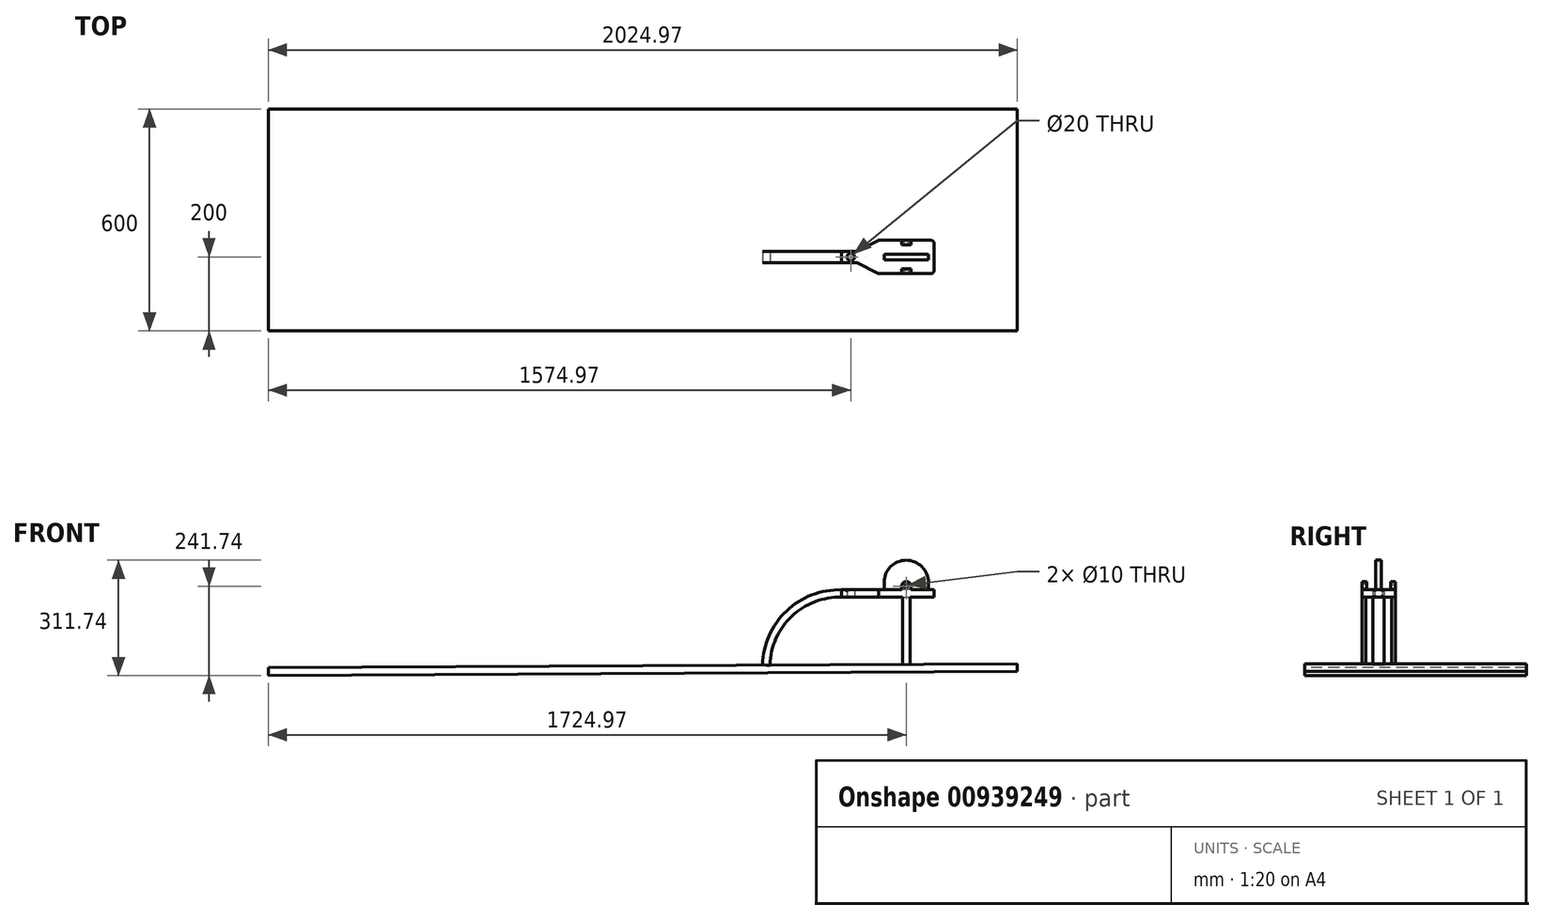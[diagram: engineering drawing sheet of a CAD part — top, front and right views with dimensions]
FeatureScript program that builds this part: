
annotation { "Feature Type Name" : "Feature", "Feature Type Description" : "" }
export const myFeature = defineFeature(function(context is Context, id is Id, definition is map)
    precondition{}
    {
        {
            var Q0;
            Q0=qCreatedBy(makeId("Right.planeOp"),FACE);
            var sketch = newSketch(context, id + "F0", { "sketchPlane" : qUnion([Q0])});
            skLineSegment(sketch, "E0", {"start": v(0, 10) * mm, "end": v(45, 10) * mm});
            skLineSegment(sketch, "E1", {"start": v(45, 10) * mm, "end": v(45, -10) * mm});
            skLineSegment(sketch, "E2", {"start": v(45, -10) * mm, "end": v(-45, -10) * mm});
            skLineSegment(sketch, "E3", {"start": v(-45, -10) * mm, "end": v(-45, 10) * mm});
            skLineSegment(sketch, "E4", {"start": v(-45, 10) * mm, "end": v(0, 10) * mm});
            skSolve(sketch);
        }
        {
            var Q0;
            Q0=makeQuery(id+"F0.imprint","IMPRINT",FACE,{"disambiguationData":[TD([[makeQuery(id+"F0.imprint","IMPRINT",EDGE,{"derivedFrom":sQuery(id+"F0.wireOp",EDGE,"E0")}),-1.0]])]});
            extrude(context, id + "F1", {"entities" : qUnion([Q0]), "depth" : 150 * mm, "offsetDistance" : 25 * mm});
        }
        {
            var Q0;
            Q0=makeQuery(id+"F1.opExtrude","SWEPT_FACE",FACE,{"disambiguationData":[OSD([sQuery(id+"F0.wireOp",EDGE,"E3")])]});
            cPlane(context, id + "F2", {"entities" : qUnion([Q0]), "cplaneType" : CPlaneType.OFFSET, "offset" : 0 * mm, "width" : 150 * mm, "height" : 150 * mm});
        }
        {
            var Q0;
            Q0=qCreatedBy(id+"F2.planeOp",FACE);
            var sketch = newSketch(context, id + "F3", { "sketchPlane" : qUnion([Q0])});
            skLineSegment(sketch, "E5", {"start": v(0, 0) * mm, "end": v(75, 0) * mm});
            skLineSegment(sketch, "E6", {"start": v(75, 0) * mm, "end": v(75, 10) * mm});
            skArc(sketch, "E7", {"start": v(87.5, 20) * mm, "mid": v(75, 32.5) * mm, "end": v(62.5, 20) * mm});
            skLineSegment(sketch, "E8", {"start": v(87.5, 20) * mm, "end": v(87.5, 10) * mm});
            skLineSegment(sketch, "E9", {"start": v(62.5, 20) * mm, "end": v(62.5, 10) * mm});
            skLineSegment(sketch, "E10", {"start": v(62.5, 10) * mm, "end": v(87.5, 10) * mm});
            skCircle(sketch, "E11", {"center": v(75, 20) * mm, "radius": 5 * mm});
            skSolve(sketch);
        }
        {
            var Q0;
            Q0=makeQuery(id+"F3.imprint","IMPRINT",FACE,{"disambiguationData":[TD([[makeQuery(id+"F3.imprint","IMPRINT",EDGE,{"derivedFrom":sQuery(id+"F3.wireOp",EDGE,"E7")}),1.0]])]});
            extrude(context, id + "F4", {"entities" : qUnion([Q0]), "operationType" : NewBodyOperationType.ADD, "oppositeDirection" : true, "depth" : 12.5 * mm, "offsetDistance" : 25 * mm});
        }
        {
            var Q0;
            Q0=makeQuery(id+"F1.opExtrude","SWEPT_FACE",FACE,{"disambiguationData":[OSD([sQuery(id+"F0.wireOp",EDGE,"E1")])]});
            cPlane(context, id + "F5", {"entities" : qUnion([Q0]), "cplaneType" : CPlaneType.OFFSET, "offset" : 0 * mm, "width" : 150 * mm, "height" : 150 * mm});
        }
        {
            var Q0;
            Q0=qCreatedBy(id+"F5.planeOp",FACE);
            var sketch = newSketch(context, id + "F6", { "sketchPlane" : qUnion([Q0])});
            skLineSegment(sketch, "E12", {"start": v(0, 0) * mm, "end": v(-75, 0) * mm});
            skLineSegment(sketch, "E13", {"start": v(-75, 0) * mm, "end": v(-75, 10) * mm});
            skArc(sketch, "E14", {"start": v(-62.5, 20) * mm, "mid": v(-75, 32.5) * mm, "end": v(-87.5, 20) * mm});
            skCircle(sketch, "E15", {"center": v(-75, 20) * mm, "radius": 5 * mm});
            skLineSegment(sketch, "E16", {"start": v(-87.5, 20) * mm, "end": v(-87.5, 10) * mm});
            skLineSegment(sketch, "E17", {"start": v(-62.5, 20) * mm, "end": v(-62.5, 10) * mm});
            skLineSegment(sketch, "E18", {"start": v(-87.5, 10) * mm, "end": v(-62.5, 10) * mm});
            skSolve(sketch);
        }
        {
            var Q0;
            Q0=makeQuery(id+"F6.imprint","IMPRINT",FACE,{"disambiguationData":[TD([[makeQuery(id+"F6.imprint","IMPRINT",EDGE,{"derivedFrom":sQuery(id+"F6.wireOp",EDGE,"E14")}),1.0]])]});
            extrude(context, id + "F7", {"entities" : qUnion([Q0]), "operationType" : NewBodyOperationType.ADD, "oppositeDirection" : true, "depth" : 12.5 * mm, "offsetDistance" : 25 * mm});
        }
        {
            var Q0;
            Q0=qCreatedBy(id+"F5.planeOp",FACE);
            cPlane(context, id + "F8", {"entities" : qUnion([Q0]), "cplaneType" : CPlaneType.OFFSET, "offset" : 45 * mm, "oppositeDirection" : true, "width" : 150 * mm, "height" : 150 * mm});
        }
        {
            var Q0;
            Q0=qCreatedBy(id+"F8.planeOp",FACE);
            var sketch = newSketch(context, id + "F9", { "sketchPlane" : qUnion([Q0])});
            skLineSegment(sketch, "E19", {"start": v(0, 0) * mm, "end": v(-75, 0) * mm});
            skLineSegment(sketch, "E20", {"start": v(-75, 0) * mm, "end": v(-75, 10) * mm});
            skLineSegment(sketch, "E21", {"start": v(-15, 30) * mm, "end": v(-15, 10) * mm});
            skLineSegment(sketch, "E22", {"start": v(-135, 30) * mm, "end": v(-135, 10) * mm});
            skLineSegment(sketch, "E23", {"start": v(-135, 10) * mm, "end": v(-15, 10) * mm});
            skArc(sketch, "E24.trimOffspring", {"start": v(-15, 30) * mm, "mid": v(-75, 90) * mm, "end": v(-135, 30) * mm});
            skSolve(sketch);
        }
        {
            var Q0;
            {var subQ2=sQuery(id+"F9.wireOp",EDGE,"E21");Q0=makeQuery(id+"F9.imprint","IMPRINT",FACE,{"disambiguationData":[TD([[makeQuery(id+"F9.imprint","IMPRINT",EDGE,{"derivedFrom":subQ2}),-1.0]])]});}
            extrude(context, id + "F10", {"entities" : qUnion([Q0]), "operationType" : NewBodyOperationType.ADD, "depth" : 7.5 * mm, "offsetDistance" : 25 * mm, "hasSecondDirection" : true, "secondDirectionOppositeDirection" : true, "secondDirectionDepth" : 7.5 * mm});
        }
        {
            var Q0;
            Q0=qCreatedBy(id+"F8.planeOp",FACE);
            var sketch = newSketch(context, id + "F11", { "sketchPlane" : qUnion([Q0])});
            skLineSegment(sketch, "E25", {"start": v(0, 0) * mm, "end": v(-75, 0) * mm});
            skLineSegment(sketch, "E26", {"start": v(-375, -190) * mm, "end": v(-375, -210) * mm});
            skLineSegment(sketch, "E27", {"start": v(1649.97, -200) * mm, "end": v(1649.84, -221.74) * mm});
            skLineSegment(sketch, "E28", {"start": v(-375, -210) * mm, "end": v(1649.84, -221.74) * mm});
            skLineSegment(sketch, "E29", {"start": v(1649.97, -200) * mm, "end": v(-375, -190) * mm});
            skLineSegment(sketch, "E30", {"start": v(0, 0) * mm, "end": v(100, 0) * mm});
            skArc(sketch, "E31", {"start": v(303.27, -193.35) * mm, "mid": v(241.95, -54.3) * mm, "end": v(100, 0) * mm});
            skSolve(sketch);
        }
        {
            var Q0;
            {var subQ0=sQuery(id+"F11.wireOp",EDGE,"E26");Q0=makeQuery(id+"F11.imprint","IMPRINT",FACE,{"disambiguationData":[TD([[makeQuery(id+"F11.imprint","IMPRINT",EDGE,{"derivedFrom":subQ0}),1.0]])]});}
            extrude(context, id + "F12", {"entities" : qUnion([Q0]), "operationType" : NewBodyOperationType.ADD, "depth" : 400 * mm, "offsetDistance" : 25 * mm, "hasSecondDirection" : true, "secondDirectionOppositeDirection" : true, "secondDirectionDepth" : 200 * mm});
        }
        {
            var Q0;
            Q0=makeQuery(id+"F1.opExtrude","SWEPT_FACE",FACE,{"disambiguationData":[OSD([sQuery(id+"F0.wireOp",EDGE,"E2")])]});
            cPlane(context, id + "F13", {"entities" : qUnion([Q0]), "cplaneType" : CPlaneType.OFFSET, "offset" : 0 * mm, "width" : 150 * mm, "height" : 150 * mm});
        }
        {
            var Q0;
            Q0=qCreatedBy(id+"F13.planeOp",FACE);
            var sketch = newSketch(context, id + "F14", { "sketchPlane" : qUnion([Q0])});
            skLineSegment(sketch, "E32", {"start": v(65, -35) * mm, "end": v(65, -45) * mm});
            skLineSegment(sketch, "E33.bottom", {"start": v(65, -45) * mm, "end": v(85, -45) * mm});
            skLineSegment(sketch, "E33.top", {"start": v(65, -35) * mm, "end": v(85, -35) * mm});
            skLineSegment(sketch, "E33.left", {"start": v(65, -45) * mm, "end": v(65, -35) * mm});
            skLineSegment(sketch, "E33.right", {"start": v(85, -45) * mm, "end": v(85, -35) * mm});
            skLineSegment(sketch, "E34.MirrorCS", {"start": v(65, 35) * mm, "end": v(65, 45) * mm});
            skLineSegment(sketch, "E35.MirrorCS", {"start": v(85, 45) * mm, "end": v(85, 35) * mm});
            skLineSegment(sketch, "E36.MirrorCS", {"start": v(65, 35) * mm, "end": v(85, 35) * mm});
            skLineSegment(sketch, "E37", {"start": v(65, 45) * mm, "end": v(85, 45) * mm});
            skSolve(sketch);
        }
        {
            var Q0;
            Q0=makeQuery(id+"F14.imprint","IMPRINT",FACE,{"disambiguationData":[TD([[makeQuery(id+"F14.imprint","IMPRINT",EDGE,{"derivedFrom":sQuery(id+"F14.wireOp",EDGE,"e01r8d7w-v4Am-usqp-IDGd-R0gfzUCGJj9g")}),1.0]])]});
            var Q1;
            Q1=makeQuery(id+"F14.imprint","IMPRINT",FACE,{"disambiguationData":[TD([[makeQuery(id+"F14.imprint","IMPRINT",EDGE,{"derivedFrom":sQuery(id+"F14.wireOp",EDGE,"E34.MirrorCS")}),-1.0]])]});
            var Q2;
            Q2=makeQuery(id+"F14.imprint","IMPRINT",FACE,{"disambiguationData":[TD([[makeQuery(id+"F14.imprint","IMPRINT",EDGE,{"derivedFrom":sQuery(id+"F14.wireOp",EDGE,"E33.bottom")}),1.0]])]});
            extrude(context, id + "F15", {"entities" : qUnion([Q0, Q1, Q2]), "operationType" : NewBodyOperationType.ADD, "depth" : 190 * mm, "offsetDistance" : 25 * mm});
        }
        {
            var Q0;
            Q0=qCreatedBy(id+"F13.planeOp",FACE);
            var sketch = newSketch(context, id + "F16", { "sketchPlane" : qUnion([Q0])});
            skCircle(sketch, "E38", {"center": v(-75, 0) * mm, "radius": 10 * mm});
            skLineSegment(sketch, "E39", {"start": v(0, 0) * mm, "end": v(0, 45.12) * mm});
            skLineSegment(sketch, "E40", {"start": v(0, 0) * mm, "end": v(0, -45.12) * mm});
            skLineSegment(sketch, "E41", {"start": v(-59.94, 15) * mm, "end": v(0, 45.12) * mm});
            skLineSegment(sketch, "E42", {"start": v(-60.16, -15.04) * mm, "end": v(0, -45.12) * mm});
            skLineSegment(sketch, "E43", {"start": v(-59.94, 15) * mm, "end": v(-85, 15) * mm});
            skLineSegment(sketch, "E44", {"start": v(-60.16, -15.04) * mm, "end": v(-85, -15.04) * mm});
            skLineSegment(sketch, "E45", {"start": v(-85, 15) * mm, "end": v(-100, 15) * mm});
            skLineSegment(sketch, "E46", {"start": v(-85, -15.04) * mm, "end": v(-100, -15.04) * mm});
            skLineSegment(sketch, "E47", {"start": v(-100, 0) * mm, "end": v(-100, 15) * mm});
            skLineSegment(sketch, "E48", {"start": v(-100, 0) * mm, "end": v(-100, -15.04) * mm});
            skSolve(sketch);
        }
        {
            var Q0;
            Q0=makeQuery(id+"F16.imprint","IMPRINT",FACE,{"disambiguationData":[TD([[makeQuery(id+"F16.imprint","IMPRINT",EDGE,{"derivedFrom":sQuery(id+"F16.wireOp",EDGE,"E38")}),-1.0]])]});
            extrude(context, id + "F17", {"entities" : qUnion([Q0]), "operationType" : NewBodyOperationType.ADD, "oppositeDirection" : true, "depth" : 20 * mm, "offsetDistance" : 25 * mm});
        }
        {
            var Q0;
            Q0=makeQuery(id+"F17.opExtrude","SWEPT_FACE",FACE,{"disambiguationData":[OSD([sQuery(id+"F16.wireOp",EDGE,"E47"),sQuery(id+"F16.wireOp",EDGE,"E48")])]});
            cPlane(context, id + "F18", {"entities" : qUnion([Q0]), "cplaneType" : CPlaneType.OFFSET, "offset" : 0 * mm, "width" : 150 * mm, "height" : 150 * mm});
        }
        {
            var Q0;
            Q0=qCreatedBy(id+"F18.planeOp",FACE);
            var sketch = newSketch(context, id + "F19", { "sketchPlane" : qUnion([Q0])});
            skLineSegment(sketch, "E49.bottom", {"start": v(-15.03, 9.96) * mm, "end": v(15, 9.96) * mm});
            skLineSegment(sketch, "E49.top", {"start": v(-15.03, -10) * mm, "end": v(15, -10) * mm});
            skLineSegment(sketch, "E49.left", {"start": v(-15.03, 9.96) * mm, "end": v(-15.03, -10) * mm});
            skLineSegment(sketch, "E49.right", {"start": v(15, 9.96) * mm, "end": v(15, -10) * mm});
            skSolve(sketch);
        }
        {
            var Q0;
            Q0 = qSketchRegion(id + "F19", true);
            var Q1;
            Q1=sQuery(id+"F11.wireOp",EDGE,"E31");
            sweep(context, id + "F20", {"profiles" : qUnion([Q0]), "path" : qUnion([Q1])});
        }
        {
            var Q0;
            Q0=makeQuery(id+"F17.opExtrude","SWEPT_EDGE",EDGE,{"disambiguationData":[OSD([sQuery(id+"F16.wireOp",EDGE,"E41"),sQuery(id+"F16.wireOp",EDGE,"E43")])]});
            var Q1;
            Q1=makeQuery(id+"F17.opExtrude","SWEPT_EDGE",EDGE,{"disambiguationData":[OSD([sQuery(id+"F16.wireOp",EDGE,"E39"),sQuery(id+"F16.wireOp",EDGE,"E41")])]});
            var Q2;
            Q2=makeQuery(id+"F1.opExtrude","CAP_EDGE",EDGE,{"disambiguationData":[OSD([sQuery(id+"F0.wireOp",EDGE,"E3")])],"isStart":false});
            var Q3;
            Q3=makeQuery(id+"F1.opExtrude","CAP_EDGE",EDGE,{"disambiguationData":[OSD([sQuery(id+"F0.wireOp",EDGE,"E1")])],"isStart":false});
            var Q4;
            Q4=makeQuery(id+"F17.opExtrude","SWEPT_EDGE",EDGE,{"disambiguationData":[OSD([sQuery(id+"F16.wireOp",EDGE,"E40"),sQuery(id+"F16.wireOp",EDGE,"E42")])]});
            var Q5;
            Q5=makeQuery(id+"F17.opExtrude","SWEPT_EDGE",EDGE,{"disambiguationData":[OSD([sQuery(id+"F16.wireOp",EDGE,"E42"),sQuery(id+"F16.wireOp",EDGE,"E44")])]});
            fillet(context, id + "F21", {"entities" : qUnion([Q0, Q1, Q2, Q3, Q4, Q5]), "radius" : 8 * mm, "tangentPropagation" : true, "allowEdgeOverflow" : false});
        }
        {
            var Q0;
            Q0=makeQuery(id+"F17.opExtrude","CAP_EDGE",EDGE,{"disambiguationData":[OSD([sQuery(id+"F16.wireOp",EDGE,"E38")])],"isStart":true});
            fillet(context, id + "F22", {"entities" : qUnion([Q0]), "radius" : 5 * mm, "tangentPropagation" : true, "allowEdgeOverflow" : false});
        }
        {
            var Q0;
            Q0=makeQuery(id+"F17.opExtrude","CAP_EDGE",EDGE,{"disambiguationData":[OSD([sQuery(id+"F16.wireOp",EDGE,"E38")])],"isStart":false});
            fillet(context, id + "F23", {"entities" : qUnion([Q0]), "radius" : 5 * mm, "tangentPropagation" : true, "allowEdgeOverflow" : false});
        }
    });
